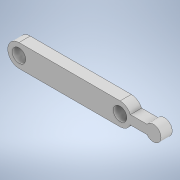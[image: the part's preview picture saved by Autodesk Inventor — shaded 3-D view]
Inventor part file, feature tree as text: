
AUTODESK INVENTOR PART (.ipt)
format: ipt  version: 2022 (Build 260153000, 153)  size: 114,688 bytes
history: native  units: mm
features: extrude x1, sketch x1
ambient origin geometry x8: Origin, YZ Plane, XZ Plane, XY Plane, X Axis, Y Axis, Z Axis, Center Point
bodies: Solid1 (feature_tree)
feature tree (2):
  extrude  "Extrusion1"  Depth=5.0mm
  sketch  "Sketch1"  dims[d0=10.0mm d1=6.0mm d3=45.0mm d4=5.0mm d5=0.0mm]
